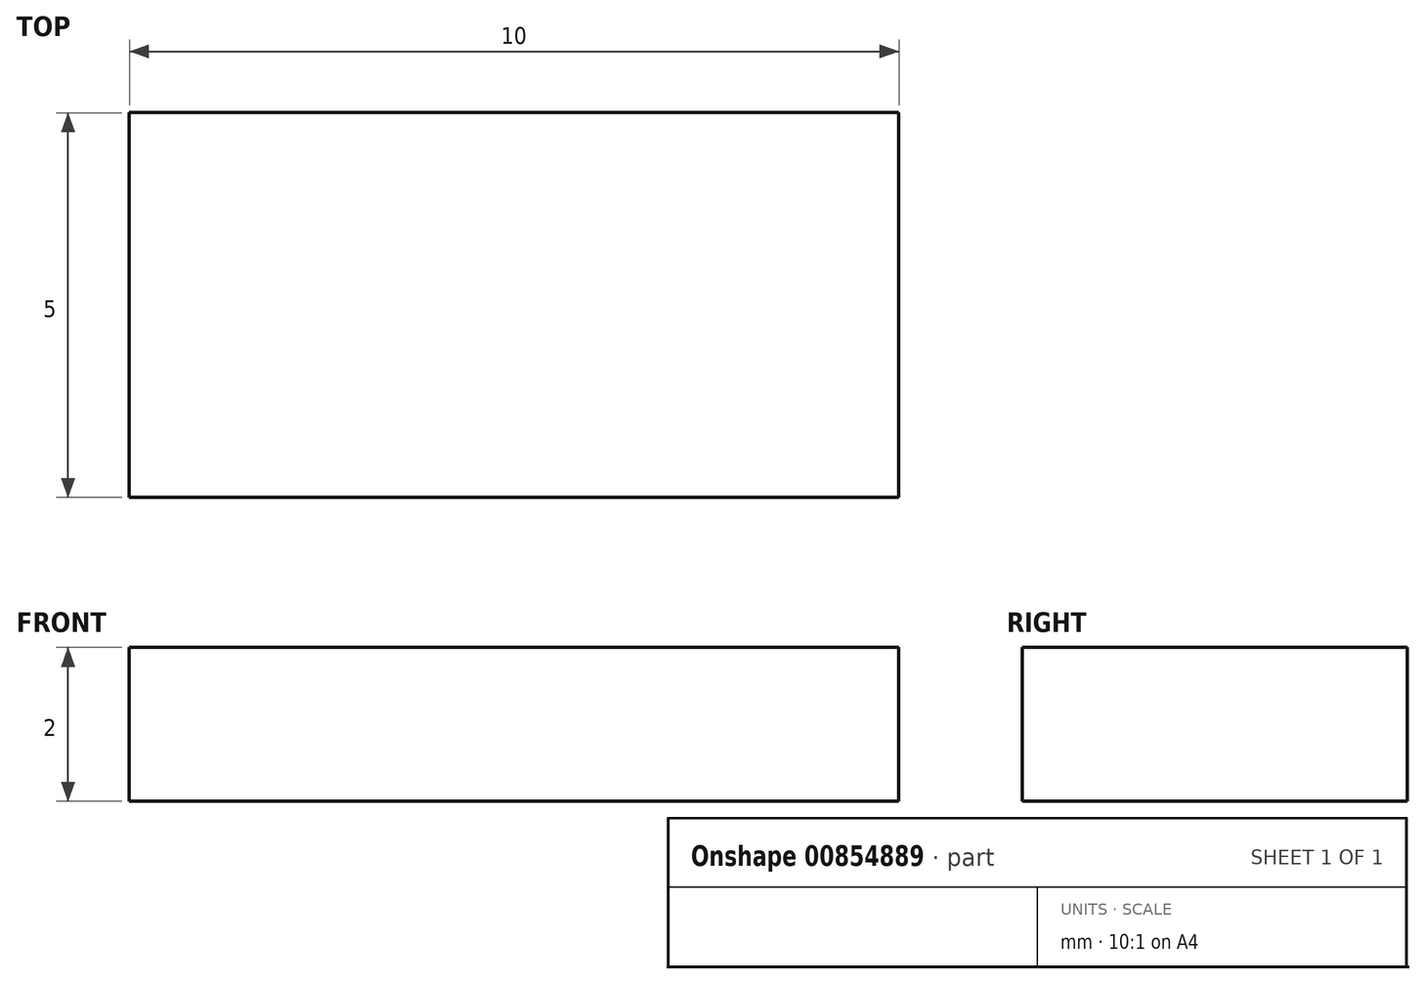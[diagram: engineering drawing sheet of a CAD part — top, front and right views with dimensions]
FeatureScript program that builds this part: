
annotation { "Feature Type Name" : "Feature", "Feature Type Description" : "" }
export const myFeature = defineFeature(function(context is Context, id is Id, definition is map)
    precondition{}
    {
        {
            var Q0;
            Q0=qCreatedBy(makeId("Top.planeOp"),FACE);
            var sketch = newSketch(context, id + "F0", { "sketchPlane" : qUnion([Q0])});
            skLineSegment(sketch, "E0.bottom", {"start": v(-94.07, -4.27) * mm, "end": v(-84.07, -4.27) * mm});
            skLineSegment(sketch, "E0.top", {"start": v(-94.07, -9.27) * mm, "end": v(-84.07, -9.27) * mm});
            skLineSegment(sketch, "E0.left", {"start": v(-94.07, -4.27) * mm, "end": v(-94.07, -9.27) * mm});
            skLineSegment(sketch, "E0.right", {"start": v(-84.07, -4.27) * mm, "end": v(-84.07, -9.27) * mm});
            skSolve(sketch);
        }
        {
            var Q0;
            Q0 = qSketchRegion(id + "F0", true);
            extrude(context, id + "F1", {"entities" : qUnion([Q0]), "depth" : 2 * mm, "offsetDistance" : 25 * mm});
        }
    });
